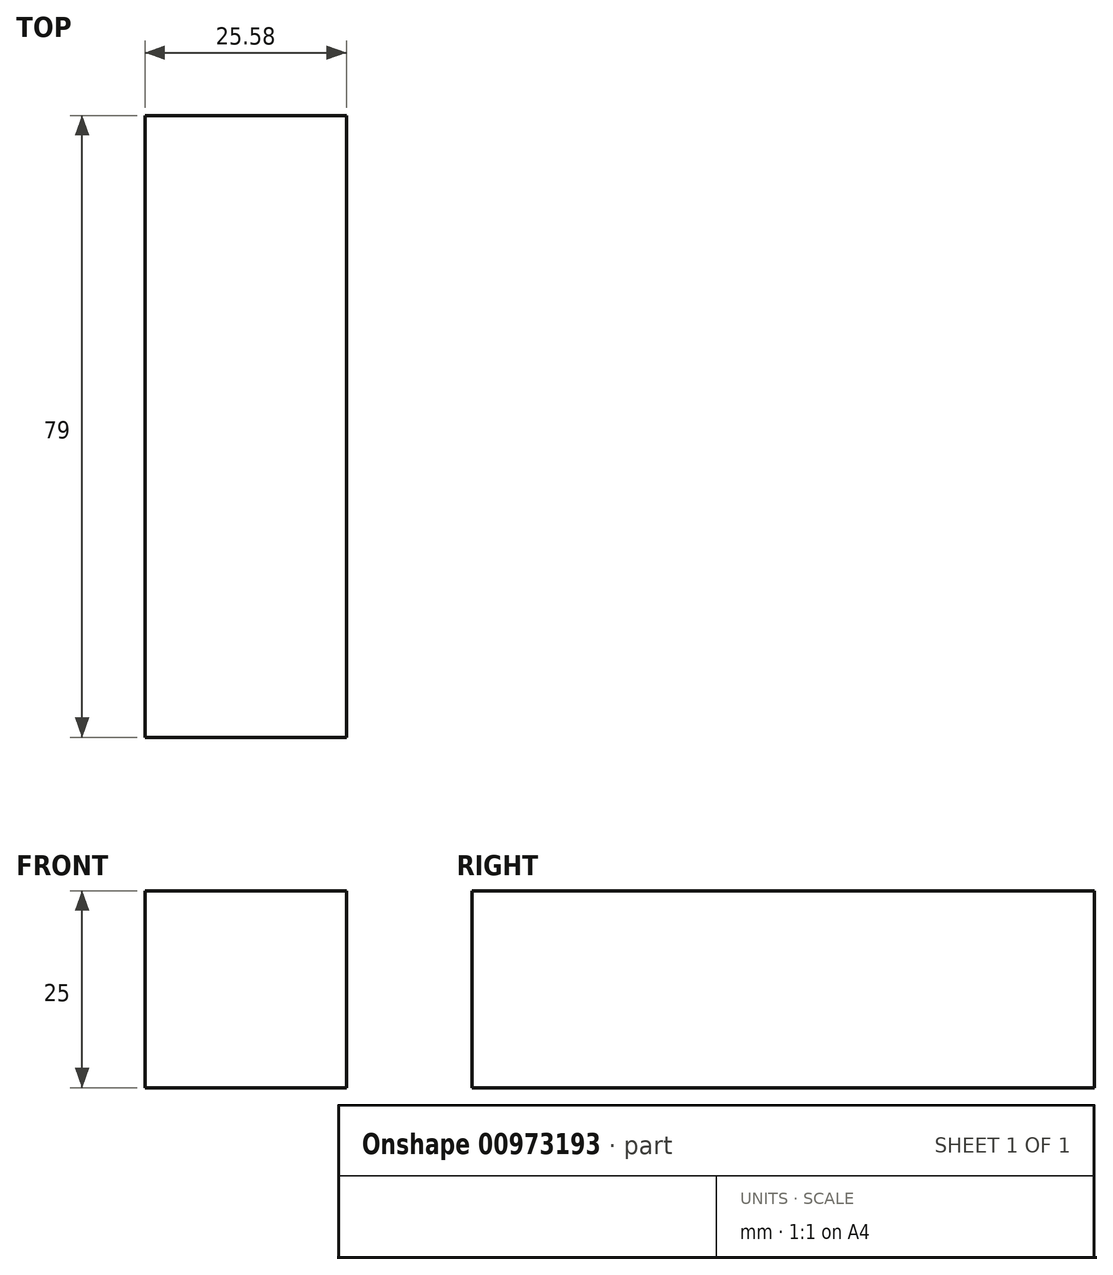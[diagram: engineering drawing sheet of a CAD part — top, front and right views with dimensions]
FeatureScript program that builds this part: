
annotation { "Feature Type Name" : "Feature", "Feature Type Description" : "" }
export const myFeature = defineFeature(function(context is Context, id is Id, definition is map)
    precondition{}
    {
        {
            var Q0;
            Q0=qCreatedBy(makeId("Top.planeOp"),FACE);
            var sketch = newSketch(context, id + "F0", { "sketchPlane" : qUnion([Q0])});
            skLineSegment(sketch, "E0.bottom", {"start": v(-23, 37.8) * mm, "end": v(2.57, 37.8) * mm});
            skLineSegment(sketch, "E0.top", {"start": v(-23, -41.2) * mm, "end": v(2.57, -41.2) * mm});
            skLineSegment(sketch, "E0.left", {"start": v(-23, 37.8) * mm, "end": v(-23, -41.2) * mm});
            skLineSegment(sketch, "E0.right", {"start": v(2.57, 37.8) * mm, "end": v(2.57, -41.2) * mm});
            skSolve(sketch);
        }
        {
            var Q0;
            Q0=makeQuery(id+"F0.imprint","IMPRINT",FACE,{"disambiguationData":[TD([[makeQuery(id+"F0.imprint","IMPRINT",EDGE,{"derivedFrom":sQuery(id+"F0.wireOp",EDGE,"E0.bottom")}),-1.0]])]});
            extrude(context, id + "F1", {"entities" : qUnion([Q0]), "depth" : 25 * mm, "offsetDistance" : 25 * mm});
        }
    });
